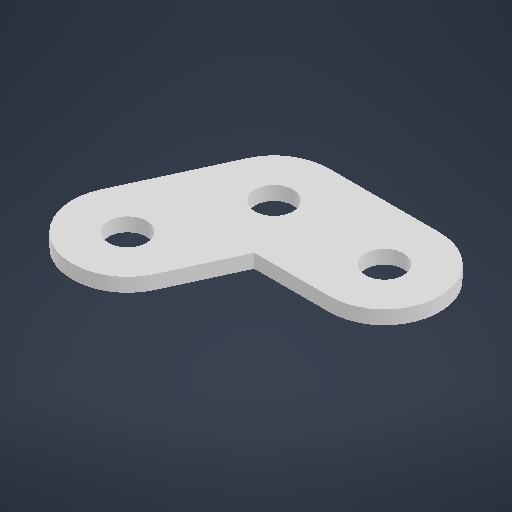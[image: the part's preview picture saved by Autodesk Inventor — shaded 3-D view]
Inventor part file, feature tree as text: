
AUTODESK INVENTOR PART (.ipt)
format: ipt  version: 2025.2 (Build 292293000, 293)  size: 192,000 bytes
history: native  units: in
note: dims shown in document units (in); Inventor stores cm internally (conversion verified against a paired STEP export)
features: extrude x1, sketch x1
ambient origin geometry x8: Origin, YZ Plane, XZ Plane, XY Plane, X Axis, Y Axis, Z Axis, Center Point
bodies: Solid1 (feature_tree)
feature tree (2):
  extrude  "Extrusion1"  Depth=0.5in
  sketch  "Sketch1"  dims[d0=0.5in d1=0.5in d2=0.5in d3=0.0625in d4=0.0in]
